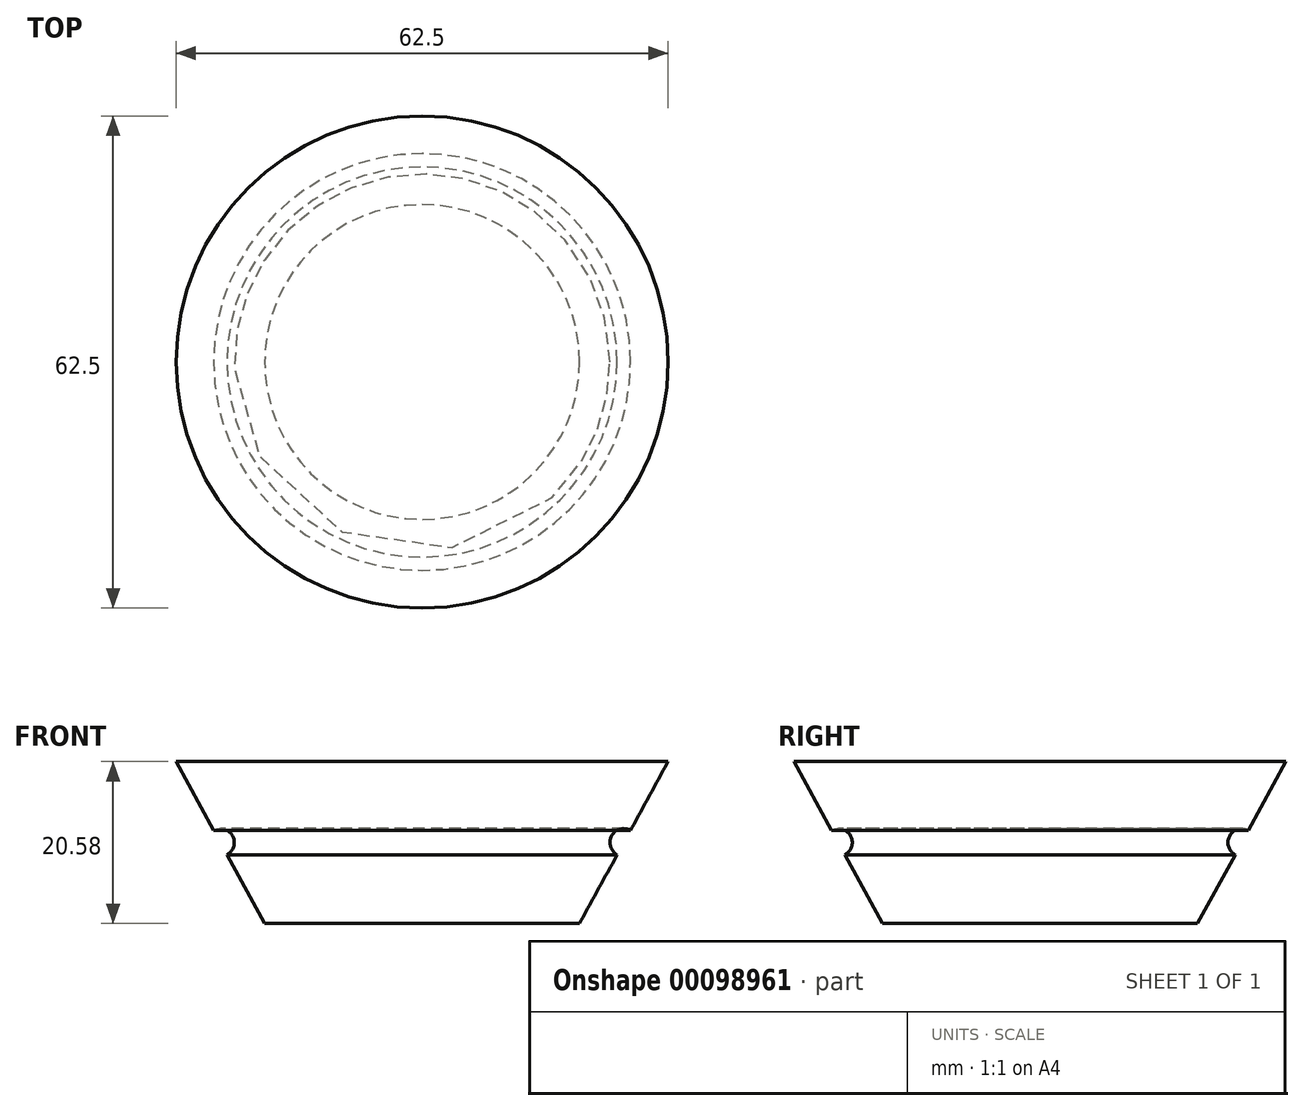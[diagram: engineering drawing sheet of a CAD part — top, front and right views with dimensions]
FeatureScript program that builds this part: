
annotation { "Feature Type Name" : "Feature", "Feature Type Description" : "" }
export const myFeature = defineFeature(function(context is Context, id is Id, definition is map)
    precondition{}
    {
        {
            var Q0;
            Q0=qCreatedBy(makeId("Front.planeOp"),FACE);
            var sketch = newSketch(context, id + "F0", { "sketchPlane" : qUnion([Q0])});
            skLineSegment(sketch, "E0", {"start": v(0, 50.08) * mm, "end": v(0, -55.64) * mm, "construction": true});
            skLineSegment(sketch, "E1", {"start": v(0, 20.58) * mm, "end": v(31.25, 20.58) * mm});
            skLineSegment(sketch, "E2", {"start": v(31.25, 20.58) * mm, "end": v(26.47, 11.84) * mm});
            skLineSegment(sketch, "E3", {"start": v(20, 0) * mm, "end": v(0, 0) * mm});
            skLineSegment(sketch, "E4", {"start": v(0, 20.58) * mm, "end": v(0, 0) * mm});
            skArc(sketch, "E5", {"start": v(26.47, 11.84) * mm, "mid": v(24.08, 11.14) * mm, "end": v(24.78, 8.74) * mm});
            skLineSegment(sketch, "E6.trimOffspring", {"start": v(24.78, 8.74) * mm, "end": v(20, 0) * mm});
            skSolve(sketch);
        }
        {
            var Q0;
            Q0=makeQuery(id+"F0.imprint","IMPRINT",FACE,{"disambiguationData":[TD([[makeQuery(id+"F0.imprint","IMPRINT",EDGE,{"derivedFrom":sQuery(id+"F0.wireOp",EDGE,"E1")}),-1.0]])]});
            var Q1;
            Q1=sQuery(id+"F0.wireOp",EDGE,"E0");
            revolve(context, id + "F1", {"entities" : qUnion([Q0]), "axis" : qUnion([Q1]), "revolveType" : RevolveType.FULL});
        }
    });
